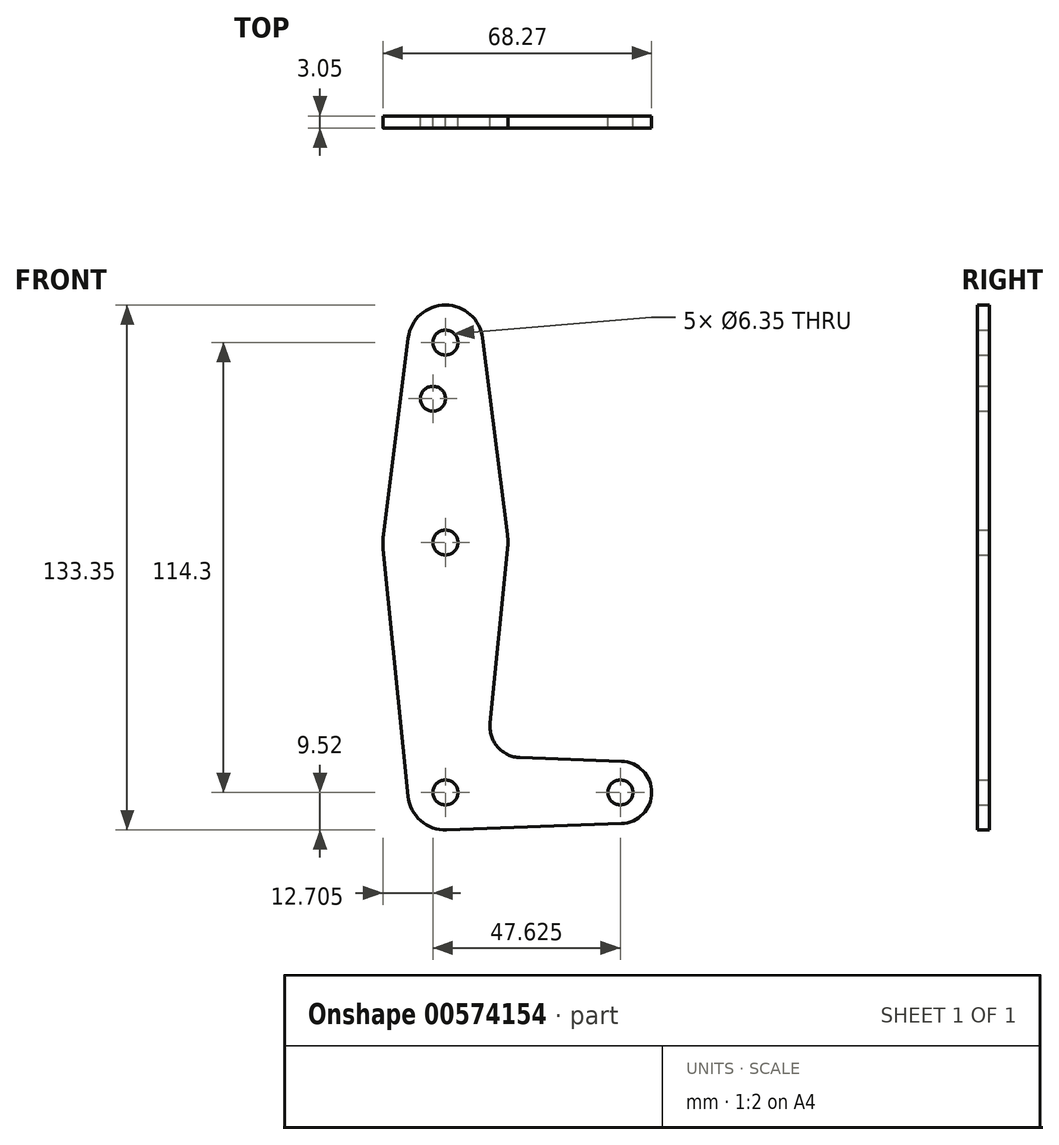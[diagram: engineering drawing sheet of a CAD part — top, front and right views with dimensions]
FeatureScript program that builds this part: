
annotation { "Feature Type Name" : "Feature", "Feature Type Description" : "" }
export const myFeature = defineFeature(function(context is Context, id is Id, definition is map)
    precondition{}
    {
        {
            var Q0;
            Q0=qCreatedBy(makeId("Front.planeOp"),FACE);
            var sketch = newSketch(context, id + "F0", { "sketchPlane" : qUnion([Q0])});
            skCircle(sketch, "E0", {"center": v(0, 0) * mm, "radius": 9.53 * mm});
            skCircle(sketch, "E1", {"center": v(0, 114.3) * mm, "radius": 9.53 * mm});
            skCircle(sketch, "E2", {"center": v(0, 63.5) * mm, "radius": 15.88 * mm});
            skCircle(sketch, "E3", {"center": v(44.45, 0) * mm, "radius": 7.94 * mm});
            skLineSegment(sketch, "E4", {"start": v(44.45, 0) * mm, "end": v(0, 0) * mm, "construction": true});
            skLineSegment(sketch, "E5", {"start": v(0, 0) * mm, "end": v(0, 63.5) * mm, "construction": true});
            skLineSegment(sketch, "E6", {"start": v(0, 63.5) * mm, "end": v(0, 114.3) * mm, "construction": true});
            skLineSegment(sketch, "E7", {"start": v(-9.45, 115.5) * mm, "end": v(-15.75, 65.48) * mm});
            skLineSegment(sketch, "E8", {"start": v(15.75, 65.48) * mm, "end": v(9.45, 115.5) * mm});
            skLineSegment(sketch, "E9", {"start": v(15.8, 61.91) * mm, "end": v(11.34, 17.6) * mm});
            skLineSegment(sketch, "E10", {"start": v(-15.8, 61.91) * mm, "end": v(-9.48, -0.95) * mm});
            skLineSegment(sketch, "E11", {"start": v(44.73, 7.93) * mm, "end": v(18.97, 8.85) * mm});
            skLineSegment(sketch, "E12", {"start": v(44.73, -7.93) * mm, "end": v(0, -9.53) * mm});
            skCircle(sketch, "E13", {"center": v(0, 114.3) * mm, "radius": 3.18 * mm});
            skCircle(sketch, "E14", {"center": v(0, 63.5) * mm, "radius": 3.18 * mm});
            skCircle(sketch, "E15", {"center": v(0, 0) * mm, "radius": 3.18 * mm});
            skCircle(sketch, "E16", {"center": v(44.45, 0) * mm, "radius": 3.18 * mm});
            skCircle(sketch, "E17", {"center": v(-3.18, 100.03) * mm, "radius": 3.18 * mm});
            skArc(sketch, "E18.filletArc", {"start": v(11.34, 17.6) * mm, "mid": v(13.26, 11.57) * mm, "end": v(18.97, 8.85) * mm});
            skSolve(sketch);
        }
        {
            var Q0;
            Q0 = qSketchRegion(id + "F0", true);
            extrude(context, id + "F1", {"entities" : qUnion([Q0]), "depth" : 3.05 * mm, "offsetDistance" : 25.4 * mm});
        }
    });
